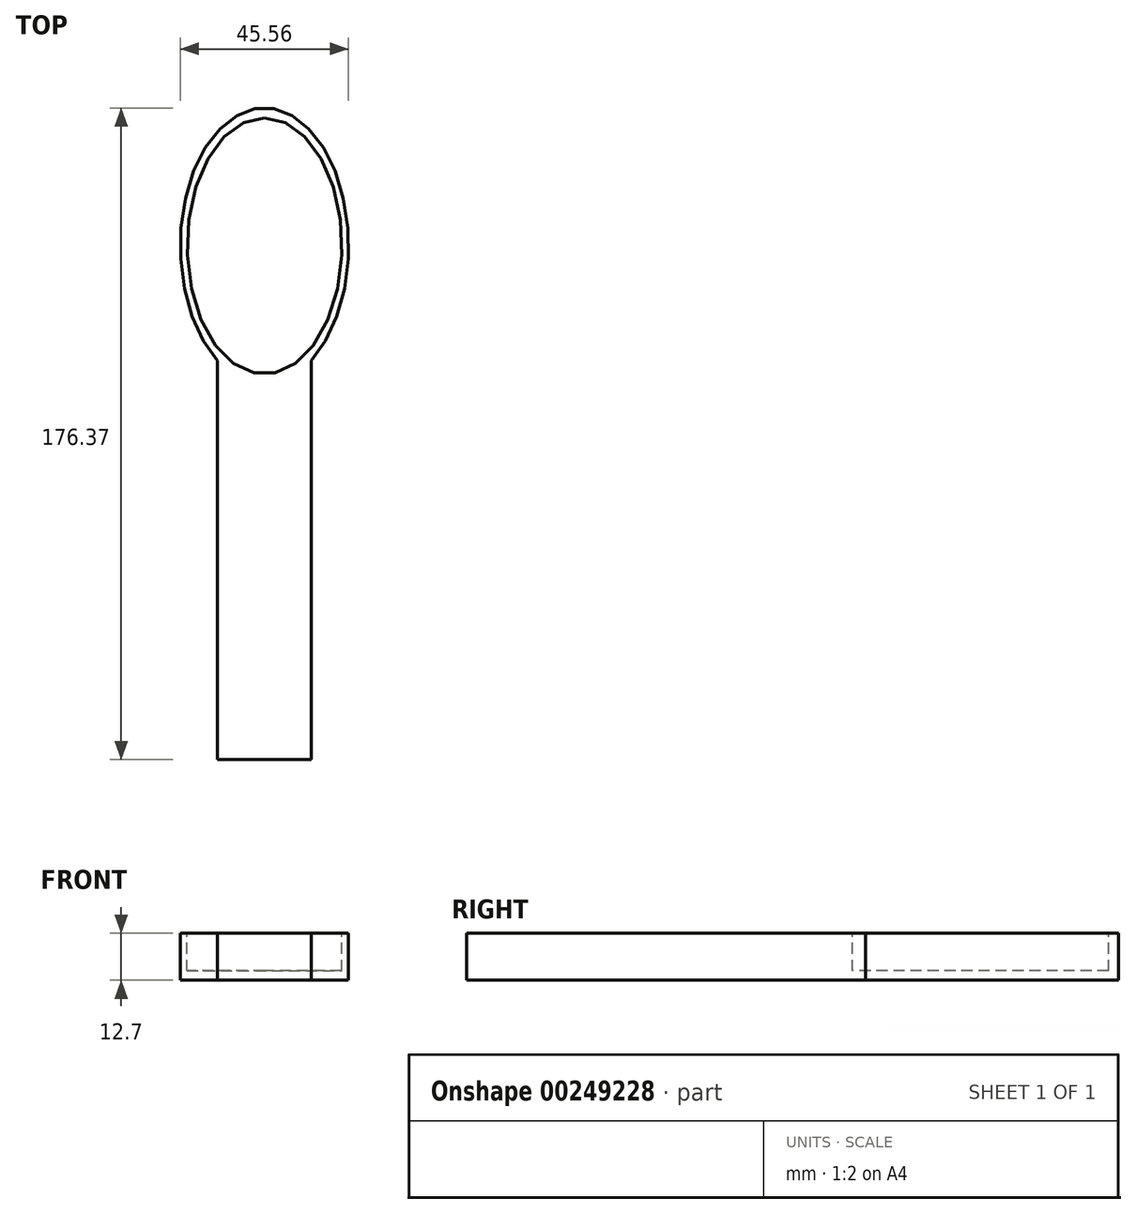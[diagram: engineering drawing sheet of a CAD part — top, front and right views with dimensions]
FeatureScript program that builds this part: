
annotation { "Feature Type Name" : "Feature", "Feature Type Description" : "" }
export const myFeature = defineFeature(function(context is Context, id is Id, definition is map)
    precondition{}
    {
        {
            var Q0;
            Q0=qCreatedBy(makeId("Top.planeOp"),FACE);
            var sketch = newSketch(context, id + "F0", { "sketchPlane" : qUnion([Q0])});
            skLineSegment(sketch, "E0", {"start": v(-12.7, -48.8) * mm, "end": v(12.7, -48.8) * mm});
            skLineSegment(sketch, "E1", {"start": v(12.7, -48.8) * mm, "end": v(12.7, 52.8) * mm});
            skLineSegment(sketch, "E2", {"start": v(-12.7, -48.8) * mm, "end": v(-12.7, 52.8) * mm});
            skLineSegment(sketch, "E3", {"start": v(-12.7, 52.8) * mm, "end": v(12.7, 52.8) * mm});
            skPoint(sketch, "E4.endSnap0", {"position": v(0, 52.8) * mm});
            skEllipse(sketch, "E5", {"center": v(0, 90.18) * mm, "majorRadius": 37.38 * mm, "minorRadius": 22.78 * mm, "majorAxis": v(0, 1)});
            skPoint(sketch, "E6.orphan", {"position": v(0, 127.56) * mm});
            skPoint(sketch, "E4.start.orphan", {"position": v(0, 52.8) * mm});
            skLineSegment(sketch, "E7", {"start": v(12.7, 52.8) * mm, "end": v(12.7, 59.14) * mm});
            skLineSegment(sketch, "E8", {"start": v(12.7, 59.14) * mm, "end": v(12.7, 52.8) * mm});
            skLineSegment(sketch, "E9", {"start": v(-12.7, 52.8) * mm, "end": v(-12.7, 59.14) * mm});
            skSolve(sketch);
        }
        {
            var Q0;
            Q0 = qSketchRegion(id + "F0", true);
            extrude(context, id + "F1", {"entities" : qUnion([Q0]), "depth" : 12.7 * mm});
        }
        {
            var Q0;
            Q0=makeQuery(id+"F1.opExtrude","CAP_FACE",FACE,{"disambiguationData":[OSD([sQuery(id+"F0.wireOp",EDGE,"E0"),sQuery(id+"F0.wireOp",EDGE,"E1"),sQuery(id+"F0.wireOp",EDGE,"E2"),sQuery(id+"F0.wireOp",EDGE,"E5"),sQuery(id+"F0.wireOp",EDGE,"E8"),sQuery(id+"F0.wireOp",EDGE,"E9")])],"isStart":false});
            var sketch = newSketch(context, id + "F2", { "sketchPlane" : qUnion([Q0])});
            skEllipse(sketch, "E10", {"center": v(0, 90.18) * mm, "majorRadius": 34.67 * mm, "minorRadius": 20.95 * mm, "majorAxis": v(0, 1)});
            skSolve(sketch);
        }
        {
            var Q0;
            Q0=makeQuery(id+"F2.imprint","IMPRINT",FACE,{"disambiguationData":[TD([[makeQuery(id+"F2.imprint","IMPRINT",EDGE,{"derivedFrom":sQuery(id+"F2.wireOp",EDGE,"E10")}),1.0]])]});
            extrude(context, id + "F3", {"entities" : qUnion([Q0]), "operationType" : NewBodyOperationType.REMOVE, "oppositeDirection" : true, "depth" : 10.16 * mm});
        }
    });
